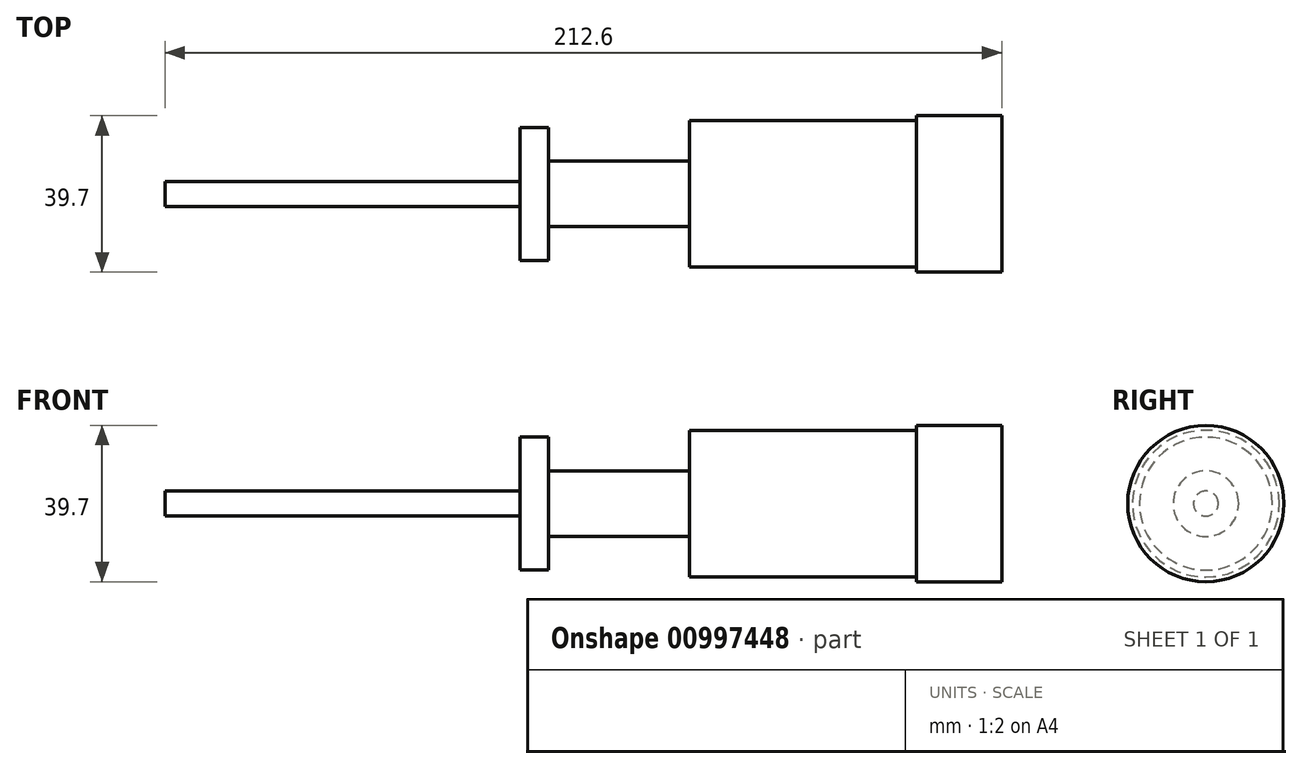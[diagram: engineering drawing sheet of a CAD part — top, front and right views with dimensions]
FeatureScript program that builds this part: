
annotation { "Feature Type Name" : "Feature", "Feature Type Description" : "" }
export const myFeature = defineFeature(function(context is Context, id is Id, definition is map)
    precondition{}
    {
        {
            var Q0;
            Q0=qCreatedBy(makeId("Front.planeOp"),FACE);
            var sketch = newSketch(context, id + "F0", { "sketchPlane" : qUnion([Q0])});
            skLineSegment(sketch, "E0", {"start": v(-90.85, 0) * mm, "end": v(121.75, 0) * mm});
            skLineSegment(sketch, "E1", {"start": v(121.75, 0) * mm, "end": v(121.75, 19.85) * mm});
            skLineSegment(sketch, "E2", {"start": v(121.75, 19.85) * mm, "end": v(100.1, 19.85) * mm});
            skLineSegment(sketch, "E3", {"start": v(100.1, 19.85) * mm, "end": v(100.1, 18.64) * mm});
            skLineSegment(sketch, "E4", {"start": v(100.1, 18.64) * mm, "end": v(42.45, 18.64) * mm});
            skLineSegment(sketch, "E5", {"start": v(42.45, 18.64) * mm, "end": v(42.45, 8.32) * mm});
            skLineSegment(sketch, "E6", {"start": v(42.45, 8.32) * mm, "end": v(6.56, 8.32) * mm});
            skLineSegment(sketch, "E7", {"start": v(6.56, 8.32) * mm, "end": v(6.56, 16.9) * mm});
            skLineSegment(sketch, "E8", {"start": v(6.56, 16.9) * mm, "end": v(-0.68, 16.9) * mm});
            skLineSegment(sketch, "E9", {"start": v(-0.68, 16.9) * mm, "end": v(-0.68, 3.18) * mm});
            skLineSegment(sketch, "E10", {"start": v(-0.68, 3.18) * mm, "end": v(-90.85, 3.17) * mm});
            skLineSegment(sketch, "E11", {"start": v(-90.85, 3.17) * mm, "end": v(-90.85, 0) * mm});
            skSolve(sketch);
        }
        {
            var Q0;
            Q0 = qSketchRegion(id + "F0", true);
            var Q1;
            Q1=sQuery(id+"F0.wireOp",EDGE,"E0");
            revolve(context, id + "F1", {"surfaceOperationType" : NewSurfaceOperationType.NEW, "entities" : qUnion([Q0]), "axis" : qUnion([Q1]), "revolveType" : RevolveType.FULL});
        }
    });
